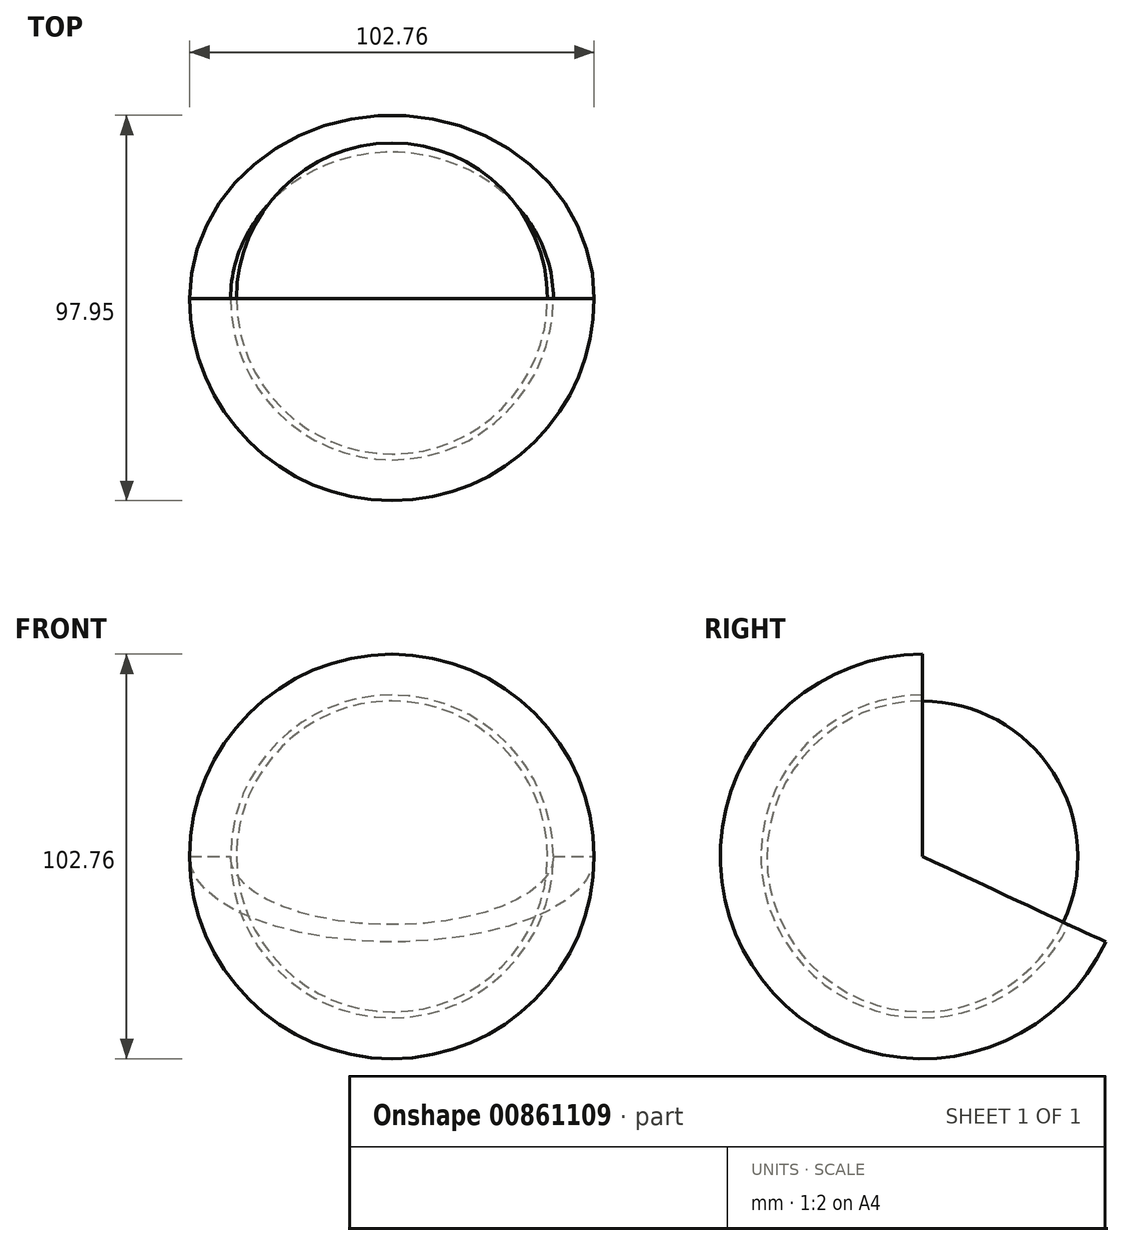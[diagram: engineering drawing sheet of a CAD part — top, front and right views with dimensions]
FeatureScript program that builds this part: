
annotation { "Feature Type Name" : "Feature", "Feature Type Description" : "" }
export const myFeature = defineFeature(function(context is Context, id is Id, definition is map)
    precondition{}
    {
        {
            var Q0;
            Q0=qCreatedBy(makeId("Front.planeOp"),FACE);
            var sketch = newSketch(context, id + "F0", { "sketchPlane" : qUnion([Q0])});
            skArc(sketch, "E0", {"start": v(51.38, 0) * mm, "mid": v(0, 51.38) * mm, "end": v(-51.38, 0) * mm});
            skArc(sketch, "E1", {"start": v(41, 0) * mm, "mid": v(0, 41) * mm, "end": v(-41, 0) * mm});
            skLineSegment(sketch, "E2", {"start": v(-51.38, 0) * mm, "end": v(-41, 0) * mm});
            skLineSegment(sketch, "E3.trimOffspring", {"start": v(41, 0) * mm, "end": v(51.38, 0) * mm});
            skSolve(sketch);
        }
        {
            var Q0;
            Q0 = qSketchRegion(id + "F0", true);
            var Q1;
            Q1=sQuery(id+"F0.wireOp",EDGE,"E2");
            revolve(context, id + "F1", {"surfaceOperationType" : NewSurfaceOperationType.NEW, "entities" : qUnion([Q0]), "axis" : qUnion([Q1]), "revolveType" : RevolveType.ONE_DIRECTION, "angle" : 245 * degree});
        }
        {
            var Q0;
            Q0=qCreatedBy(makeId("Front.planeOp"),FACE);
            var sketch = newSketch(context, id + "F2", { "sketchPlane" : qUnion([Q0])});
            skArc(sketch, "E4", {"start": v(39.5, 0) * mm, "mid": v(0, 39.5) * mm, "end": v(-39.5, 0) * mm});
            skLineSegment(sketch, "E5", {"start": v(39.5, 0) * mm, "end": v(-39.5, 0) * mm});
            skSolve(sketch);
        }
        {
            var Q0;
            Q0 = qSketchRegion(id + "F2", true);
            var Q1;
            Q1=sQuery(id+"F2.wireOp",EDGE,"E5");
            revolve(context, id + "F3", {"surfaceOperationType" : NewSurfaceOperationType.NEW, "entities" : qUnion([Q0]), "axis" : qUnion([Q1]), "revolveType" : RevolveType.FULL});
        }
    });
